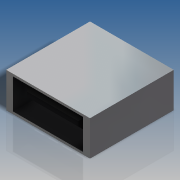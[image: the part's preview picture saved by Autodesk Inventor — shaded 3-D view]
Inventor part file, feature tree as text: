
AUTODESK INVENTOR PART (.ipt)
format: ipt  version: 2016 SP2 (Build 200236200, 236)  size: 158,208 bytes
history: native  units: in
note: dims shown in document units (in); Inventor stores cm internally (conversion verified against a paired STEP export)
features: extrude x4, sketch x3, chamfer x1
ambient origin geometry x8: Origin, YZ Plane, XZ Plane, XY Plane, X Axis, Y Axis, Z Axis, Center Point
bodies: Solid1 (feature_tree)
feature tree (8):
  extrude  "Extrusion1"  Depth=0.4724in
  sketch  "Sketch3"  dims[d2=0.5669in d3=0.0in d4=0.063in]
  extrude  "Extrusion2"  Depth=0.063in
  extrude  "Extrusion3"  Depth=0.5354in TaperAngle=0.0deg
  chamfer  "Chamfer1"  Distance=0.0315in
  extrude  "Extrusion4"  Depth=0.0157in TaperAngle=45.0deg
  sketch  "Sketch2"  dims[d0=0.2047in d1=0.4724in]
  sketch  "Sketch4"  dims[d5=0.378in d7=0.5354in d8=0.0in d12=0.0315in d13=0.0in d15=0.0157in d16=0.0787in d17=45.0deg d18=0.4559in d19=0.063in d20=0.0315in d21=0.0in d22=0.0in d23=0.2362in d24=0.5669in d25=0.0174in]
